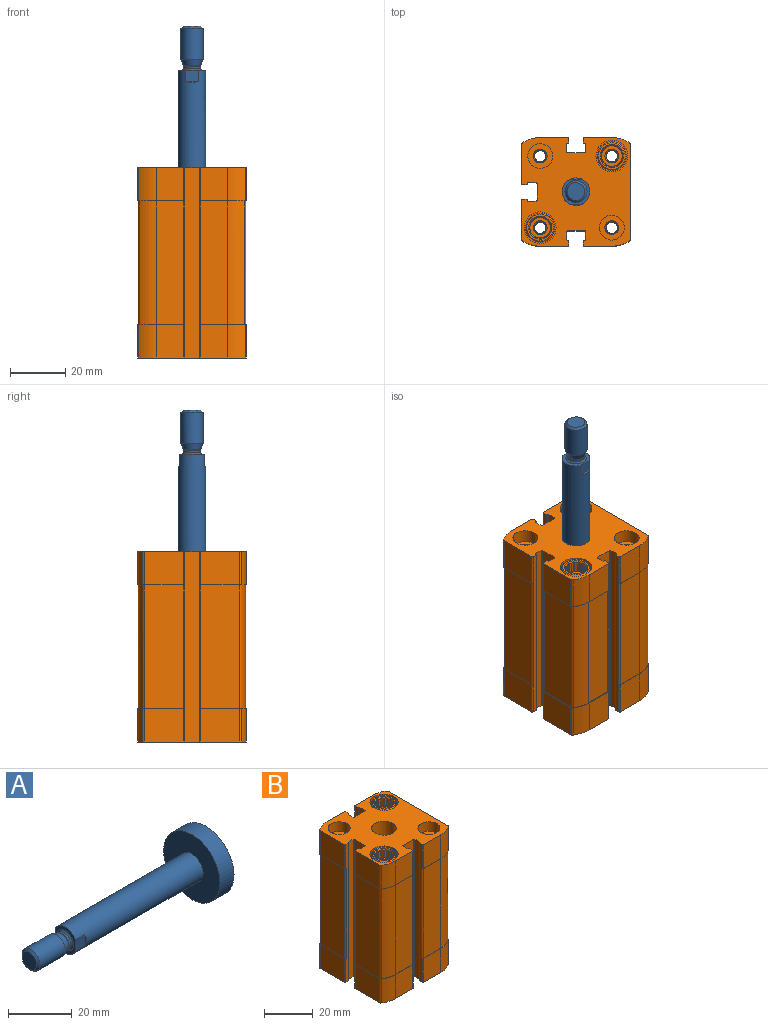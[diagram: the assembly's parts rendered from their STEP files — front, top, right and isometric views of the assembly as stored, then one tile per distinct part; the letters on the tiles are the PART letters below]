
ASSEMBLY  parts=2 mates=1
PART A: 16 faces, bbox 79.1x25.6x25.6 mm
  f0: plane 6.47x6.47mm, normal (-1,0,0), area 32.9mm2, adj f1
  f1: revolved ~8x8mm, area 24.6mm2, adj f0,f2
  f2: revolved ~11.26x8mm, area 283mm2, adj f1,f3
  f3: revolved ~8x8mm, area 56.6mm2, adj f2,f4
  f4: revolved ~6.27x6.27mm, area 4.1mm2, adj f3,f6
  f5: plane 25x25mm, normal (1,0,0), area 490.8mm2, adj f7
  f6: revolved ~6.2x6.2mm, area 15.5mm2, adj f4,f8
  f7: revolved ~25x25mm, area 490.9mm2, adj f5,f9
  f8: revolved ~7.4x7.4mm, area 19.7mm2, adj f6,f12
  f9: plane 25x25mm, normal (-1,0,0), area 412.4mm2, adj f7,f15
  f10: plane 4.94x1.08mm, normal (-0.87,0.5,0), area 1.7mm2, adj f11,f15
  f11: plane 4.36x4.2mm, normal (0,1,0), area 18.3mm2, adj f10,f12,f15
  f12: plane 10x9mm, normal (-1,0,0), area 32.6mm2, adj f8,f11,f13,f15
  f13: plane 4.36x4.2mm, normal (0,-1,0), area 18.3mm2, adj f12,f14,f15
  f14: plane 4.94x1.08mm, normal (-0.87,-0.5,0), area 1.7mm2, adj f13,f15
  f15: revolved ~56.25x10mm, area 1729.3mm2, adj f9,f10,f11,f12,f13,f14
PART B: 334 faces, bbox 39.6x39.6x69.1 mm
  f0: plane 1.01x0.59mm, normal (0,0,1), area 0.2mm2, adj f32,f33,f52
  f1: plane 1.01x0.59mm, normal (0,0,1), area 0.2mm2, adj f30,f31,f52
  f2: plane 1.17x0.34mm, normal (0,0,1), area 0.2mm2, adj f28,f29,f52
  f3: plane 1.01x0.59mm, normal (0,0,1), area 0.2mm2, adj f50,f51,f52
  f4: plane 1.01x0.59mm, normal (0,0,1), area 0.2mm2, adj f48,f49,f52
  f5: plane 1.17x0.34mm, normal (0,0,1), area 0.2mm2, adj f46,f47,f52
  f6: plane 1.01x0.59mm, normal (0,0,1), area 0.2mm2, adj f44,f45,f52
  f7: plane 1.01x0.59mm, normal (0,0,1), area 0.2mm2, adj f42,f43,f52
  f8: plane 1.17x0.34mm, normal (0,0,1), area 0.2mm2, adj f40,f41,f52
  f9: plane 1.01x0.59mm, normal (0,0,1), area 0.2mm2, adj f38,f39,f52
  f10: plane 1.01x0.59mm, normal (0,0,1), area 0.2mm2, adj f36,f37,f52
  f11: plane 1.17x0.34mm, normal (0,0,1), area 0.2mm2, adj f34,f35,f52
  f12: plane 1.01x0.59mm, normal (0,0,1), area 0.2mm2, adj f57,f58,f77
  f13: plane 1.01x0.59mm, normal (0,0,1), area 0.2mm2, adj f55,f56,f77
  f14: plane 1.17x0.34mm, normal (0,0,1), area 0.2mm2, adj f53,f54,f77
  f15: plane 1.01x0.59mm, normal (0,0,1), area 0.2mm2, adj f75,f76,f77
  f16: plane 1.01x0.59mm, normal (0,0,1), area 0.2mm2, adj f73,f74,f77
  f17: plane 1.17x0.34mm, normal (0,0,1), area 0.2mm2, adj f71,f72,f77
  f18: plane 1.01x0.59mm, normal (0,0,1), area 0.2mm2, adj f69,f70,f77
  f19: plane 1.01x0.59mm, normal (0,0,1), area 0.2mm2, adj f67,f68,f77
  f20: plane 1.17x0.34mm, normal (0,0,1), area 0.2mm2, adj f65,f66,f77
  f21: plane 1.01x0.59mm, normal (0,0,1), area 0.2mm2, adj f63,f64,f77
  f22: plane 1.01x0.59mm, normal (0,0,1), area 0.2mm2, adj f61,f62,f77
  f23: plane 1.17x0.34mm, normal (0,0,1), area 0.2mm2, adj f59,f60,f77
  f24: plane 7.5x7.5mm, normal (0,0,1), area 24.6mm2, adj f52,f78
  f25: plane 7.5x7.5mm, normal (0,0,1), area 24.6mm2, adj f77,f79
  f26: revolved ~14.47x4.13mm, area 187.9mm2, adj f27,f80
  f27: plane 5x5mm, normal (0,0,1), area 6.2mm2, adj f26,f81
  f28: plane 4.18x0.64mm, normal (0.5,-0.87,0), area 2.6mm2, adj f2,f29,f52,f82
  f29: plane 4.18x0.64mm, normal (-0.5,-0.87,0), area 2.6mm2, adj f2,f28,f52,f82
  f30: plane 4.18x0.73mm, normal (0,-1,0), area 2.6mm2, adj f1,f31,f52,f82
  f31: plane 4.18x0.64mm, normal (-0.87,-0.5,0), area 2.6mm2, adj f1,f30,f52,f82
  f32: plane 4.18x0.64mm, normal (-0.5,-0.87,0), area 2.6mm2, adj f0,f33,f52,f82
  f33: plane 4.18x0.73mm, normal (-1,0,0), area 2.6mm2, adj f0,f32,f52,f82
  f34: plane 4.18x0.64mm, normal (-0.87,-0.5,0), area 2.6mm2, adj f11,f35,f52,f82
  f35: plane 4.18x0.64mm, normal (-0.87,0.5,0), area 2.6mm2, adj f11,f34,f52,f82
  f36: plane 4.18x0.73mm, normal (-1,0,0), area 2.6mm2, adj f10,f37,f52,f82
  f37: plane 4.18x0.64mm, normal (-0.5,0.87,0), area 2.6mm2, adj f10,f36,f52,f82
  f38: plane 4.18x0.64mm, normal (-0.87,0.5,0), area 2.6mm2, adj f9,f39,f52,f82
  f39: plane 4.18x0.73mm, normal (0,1,0), area 2.6mm2, adj f9,f38,f52,f82
  f40: plane 4.18x0.64mm, normal (-0.5,0.87,0), area 2.6mm2, adj f8,f41,f52,f82
  f41: plane 4.18x0.64mm, normal (0.5,0.87,0), area 2.6mm2, adj f8,f40,f52,f82
  f42: plane 4.18x0.73mm, normal (0,1,0), area 2.6mm2, adj f7,f43,f52,f82
  f43: plane 4.18x0.64mm, normal (0.87,0.5,0), area 2.6mm2, adj f7,f42,f52,f82
  f44: plane 4.18x0.64mm, normal (0.5,0.87,0), area 2.6mm2, adj f6,f45,f52,f82
  f45: plane 4.18x0.73mm, normal (1,0,0), area 2.6mm2, adj f6,f44,f52,f82
  f46: plane 4.18x0.64mm, normal (0.87,0.5,0), area 2.6mm2, adj f5,f47,f52,f82
  f47: plane 4.18x0.64mm, normal (0.87,-0.5,0), area 2.6mm2, adj f5,f46,f52,f82
  f48: plane 4.18x0.73mm, normal (1,0,0), area 2.6mm2, adj f4,f49,f52,f82
  f49: plane 4.18x0.64mm, normal (0.5,-0.87,0), area 2.6mm2, adj f4,f48,f52,f82
  f50: plane 4.18x0.64mm, normal (0.87,-0.5,0), area 2.6mm2, adj f3,f51,f52,f82
  f51: plane 4.18x0.73mm, normal (0,-1,0), area 2.6mm2, adj f3,f50,f52,f82
  f52: revolved ~7.5x7.5mm, area 39.1mm2, adj f0,f1,f2,f3,f4,f5,f6,f7
  f53: plane 4.18x0.64mm, normal (0.5,-0.87,0), area 2.6mm2, adj f14,f54,f77,f83
  f54: plane 4.18x0.64mm, normal (-0.5,-0.87,0), area 2.6mm2, adj f14,f53,f77,f83
  f55: plane 4.18x0.73mm, normal (0,-1,0), area 2.6mm2, adj f13,f56,f77,f83
  f56: plane 4.18x0.64mm, normal (-0.87,-0.5,0), area 2.6mm2, adj f13,f55,f77,f83
  f57: plane 4.18x0.64mm, normal (-0.5,-0.87,0), area 2.6mm2, adj f12,f58,f77,f83
  f58: plane 4.18x0.73mm, normal (-1,0,0), area 2.6mm2, adj f12,f57,f77,f83
  f59: plane 4.18x0.64mm, normal (-0.87,-0.5,0), area 2.6mm2, adj f23,f60,f77,f83
  f60: plane 4.18x0.64mm, normal (-0.87,0.5,0), area 2.6mm2, adj f23,f59,f77,f83
  f61: plane 4.18x0.73mm, normal (-1,0,0), area 2.6mm2, adj f22,f62,f77,f83
  f62: plane 4.18x0.64mm, normal (-0.5,0.87,0), area 2.6mm2, adj f22,f61,f77,f83
  f63: plane 4.18x0.64mm, normal (-0.87,0.5,0), area 2.6mm2, adj f21,f64,f77,f83
  f64: plane 4.18x0.73mm, normal (0,1,0), area 2.6mm2, adj f21,f63,f77,f83
  f65: plane 4.18x0.64mm, normal (-0.5,0.87,0), area 2.6mm2, adj f20,f66,f77,f83
  f66: plane 4.18x0.64mm, normal (0.5,0.87,0), area 2.6mm2, adj f20,f65,f77,f83
  f67: plane 4.18x0.73mm, normal (0,1,0), area 2.6mm2, adj f19,f68,f77,f83
  f68: plane 4.18x0.64mm, normal (0.87,0.5,0), area 2.6mm2, adj f19,f67,f77,f83
  f69: plane 4.18x0.64mm, normal (0.5,0.87,0), area 2.6mm2, adj f18,f70,f77,f83
  f70: plane 4.18x0.73mm, normal (1,0,0), area 2.6mm2, adj f18,f69,f77,f83
  f71: plane 4.18x0.64mm, normal (0.87,0.5,0), area 2.6mm2, adj f17,f72,f77,f83
  f72: plane 4.18x0.64mm, normal (0.87,-0.5,0), area 2.6mm2, adj f17,f71,f77,f83
  f73: plane 4.18x0.73mm, normal (1,0,0), area 2.6mm2, adj f16,f74,f77,f83
  f74: plane 4.18x0.64mm, normal (0.5,-0.87,0), area 2.6mm2, adj f16,f73,f77,f83
  f75: plane 4.18x0.64mm, normal (0.87,-0.5,0), area 2.6mm2, adj f15,f76,f77,f83
  f76: plane 4.18x0.73mm, normal (0,-1,0), area 2.6mm2, adj f15,f75,f77,f83
  f77: revolved ~7.5x7.5mm, area 39.1mm2, adj f12,f13,f14,f15,f16,f17,f18,f19
  f78: revolved ~5x5mm, area 8.8mm2, adj f24,f84
  f79: revolved ~5x5mm, area 8.8mm2, adj f25,f85
  f80: revolved ~5x5mm, area 8.8mm2, adj f26,f86
  f81: revolved ~37.5x5mm, area 589mm2, adj f27,f99
  f82: revolved ~8.4x8.4mm, area 18.3mm2, adj f28,f29,f30,f31,f32,f33,f34,f35
  f83: revolved ~8.4x8.4mm, area 18.3mm2, adj f53,f54,f55,f56,f57,f58,f59,f60
  f84: revolved ~14.47x4.13mm, area 187.9mm2, adj f78,f102
  f85: revolved ~14.47x4.13mm, area 187.9mm2, adj f79,f103
  f86: plane 7.5x7.5mm, normal (0,0,-1), area 24.5mm2, adj f80,f126
  f87: plane 1.01x0.59mm, normal (0,0,-1), area 0.2mm2, adj f124,f125,f126
  f88: plane 1.17x0.34mm, normal (0,0,-1), area 0.2mm2, adj f122,f123,f126
  f89: plane 1.01x0.59mm, normal (0,0,-1), area 0.2mm2, adj f120,f121,f126
  f90: plane 1.01x0.59mm, normal (0,0,-1), area 0.2mm2, adj f118,f119,f126
  f91: plane 1.17x0.34mm, normal (0,0,-1), area 0.2mm2, adj f116,f117,f126
  f92: plane 1.01x0.59mm, normal (0,0,-1), area 0.2mm2, adj f114,f115,f126
  f93: plane 1.01x0.59mm, normal (0,0,-1), area 0.2mm2, adj f112,f113,f126
  f94: plane 1.17x0.34mm, normal (0,0,-1), area 0.2mm2, adj f110,f111,f126
  f95: plane 1.01x0.59mm, normal (0,0,-1), area 0.2mm2, adj f108,f109,f126
  f96: plane 1.01x0.59mm, normal (0,0,-1), area 0.2mm2, adj f106,f107,f126
  f97: plane 1.17x0.34mm, normal (0,0,-1), area 0.2mm2, adj f104,f105,f126
  f98: plane 1.01x0.59mm, normal (0,0,-1), area 0.2mm2, adj f126,f127,f128
  f99: plane 5x5mm, normal (0,0,-1), area 6.2mm2, adj f81,f130
  f100: plane 9.7x9.7mm, normal (0,0,1), area 18.5mm2, adj f82,f131
  f101: plane 9.7x9.7mm, normal (0,0,1), area 18.5mm2, adj f83,f132
  f102: plane 5x5mm, normal (0,0,-1), area 6.2mm2, adj f84,f134
  f103: plane 5x5mm, normal (0,0,-1), area 6.2mm2, adj f85,f135
  f104: plane 4.18x0.64mm, normal (0.87,-0.5,0), area 2.6mm2, adj f97,f105,f126,f136
  f105: plane 4.18x0.64mm, normal (0.87,0.5,0), area 2.6mm2, adj f97,f104,f126,f136
  f106: plane 4.18x0.73mm, normal (1,0,0), area 2.6mm2, adj f96,f107,f126,f136
  f107: plane 4.18x0.64mm, normal (0.5,0.87,0), area 2.6mm2, adj f96,f106,f126,f136
  f108: plane 4.18x0.64mm, normal (0.87,0.5,0), area 2.6mm2, adj f95,f109,f126,f136
  f109: plane 4.18x0.73mm, normal (0,1,0), area 2.6mm2, adj f95,f108,f126,f136
  f110: plane 4.18x0.64mm, normal (0.5,0.87,0), area 2.6mm2, adj f94,f111,f126,f136
  f111: plane 4.18x0.64mm, normal (-0.5,0.87,0), area 2.6mm2, adj f94,f110,f126,f136
  f112: plane 4.18x0.73mm, normal (0,1,0), area 2.6mm2, adj f93,f113,f126,f136
  f113: plane 4.18x0.64mm, normal (-0.87,0.5,0), area 2.6mm2, adj f93,f112,f126,f136
  f114: plane 4.18x0.64mm, normal (-0.5,0.87,0), area 2.6mm2, adj f92,f115,f126,f136
  f115: plane 4.18x0.73mm, normal (-1,0,0), area 2.6mm2, adj f92,f114,f126,f136
  f116: plane 4.18x0.64mm, normal (-0.87,0.5,0), area 2.6mm2, adj f91,f117,f126,f136
  f117: plane 4.18x0.64mm, normal (-0.87,-0.5,0), area 2.6mm2, adj f91,f116,f126,f136
  f118: plane 4.18x0.73mm, normal (-1,0,0), area 2.6mm2, adj f90,f119,f126,f136
  f119: plane 4.18x0.64mm, normal (-0.5,-0.87,0), area 2.6mm2, adj f90,f118,f126,f136
  f120: plane 4.18x0.64mm, normal (-0.87,-0.5,0), area 2.6mm2, adj f89,f121,f126,f136
  f121: plane 4.18x0.73mm, normal (0,-1,0), area 2.6mm2, adj f89,f120,f126,f136
  f122: plane 4.18x0.64mm, normal (-0.5,-0.87,0), area 2.6mm2, adj f88,f123,f126,f136
  f123: plane 4.18x0.64mm, normal (0.5,-0.87,0), area 2.6mm2, adj f88,f122,f126,f136
  f124: plane 4.18x0.73mm, normal (0,-1,0), area 2.6mm2, adj f87,f125,f126,f136
  f125: plane 4.18x0.64mm, normal (0.87,-0.5,0), area 2.6mm2, adj f87,f124,f126,f136
  f126: revolved ~7.5x7.5mm, area 39.1mm2, adj f86,f87,f88,f89,f90,f91,f92,f93
  f127: plane 4.18x0.64mm, normal (0.5,-0.87,0), area 2.6mm2, adj f98,f126,f128,f136
  f128: plane 4.18x0.73mm, normal (1,0,0), area 2.6mm2, adj f98,f126,f127,f136
  f129: plane 4.14x4.14mm, normal (1,0,0), area 13.4mm2, adj f137
  f130: revolved ~6.77x4.13mm, area 87.9mm2, adj f99,f138
  f131: revolved ~10.5x10.5mm, area 17.9mm2, adj f100,f139
  f132: revolved ~10.5x10.5mm, area 17.9mm2, adj f101,f140
  f133: plane 25x25mm, normal (0,0,1), area 490.9mm2, adj f141
  f134: revolved ~37.5x5mm, area 589mm2, adj f102,f142
  f135: revolved ~37.5x5mm, area 589mm2, adj f103,f143
  f136: revolved ~8.4x8.4mm, area 18.3mm2, adj f104,f105,f106,f107,f108,f109,f110,f111
  f137: revolved ~10.57x4.13mm, area 137.2mm2, adj f129,f146
  f138: revolved ~5x5mm, area 8.8mm2, adj f130,f147
  f139: revolved ~10.5x10.5mm, area 201.2mm2, adj f131,f148
  f140: revolved ~10.5x10.5mm, area 201.2mm2, adj f132,f149
  f141: revolved ~36.25x25mm, area 2847.1mm2, adj f133,f150
  f142: plane 5x5mm, normal (0,0,1), area 6.2mm2, adj f134,f151
  f143: plane 5x5mm, normal (0,0,1), area 6.2mm2, adj f135,f152
  f144: plane 9.7x9.7mm, normal (0,0,-1), area 18.5mm2, adj f136,f153
  f145: plane 4.14x4.14mm, normal (1,0,0), area 13.4mm2, adj f159
  f146: revolved ~5x5mm, area 8.8mm2, adj f137,f174
  f147: plane 9x9mm, normal (0,0,1), area 44mm2, adj f138,f182
  f148: plane 11.5x11.5mm, normal (0,0,1), area 17.3mm2, adj f139,f184
  f149: plane 11.5x11.5mm, normal (0,0,1), area 17.3mm2, adj f140,f185
  f150: plane 25x25mm, normal (0,0,-1), area 412.3mm2, adj f141,f186
  f151: revolved ~6.77x4.13mm, area 87.9mm2, adj f142,f193
  f152: revolved ~6.77x4.13mm, area 87.9mm2, adj f143,f194
  f153: revolved ~10.5x10.5mm, area 35.9mm2, adj f144,f195
  f154: plane 45x13.99mm, normal (-1,0,0), area 629.6mm2, adj f155,f157,f199,f201
  f155: revolved ~45x0.68mm, area 36.7mm2, adj f154,f156,f157,f201
  f156: revolved ~45x6.12mm, area 289.7mm2, adj f155,f157,f158,f201
  f157: plane 17.05x17.05mm, normal (0,0,-1), area 8mm2, adj f154,f155,f156,f158,f178,f179,f180,f181
  f158: plane 45x9.9mm, normal (0,1,0), area 445.5mm2, adj f156,f157,f201,f203
  f159: revolved ~10.57x4.13mm, area 137.2mm2, adj f145,f206
  f160: plane 45x9.9mm, normal (0,1,0), area 445.5mm2, adj f161,f166,f204,f207
  f161: revolved ~45x6.12mm, area 289.7mm2, adj f160,f162,f166,f207
  f162: revolved ~45x0.68mm, area 36.7mm2, adj f161,f163,f166,f207
  f163: plane 45x34.18mm, normal (1,0,0), area 1538.2mm2, adj f162,f164,f166,f207
  f164: revolved ~45x0.68mm, area 36.7mm2, adj f163,f165,f166,f207
  f165: revolved ~45x6.12mm, area 289.7mm2, adj f164,f166,f167,f207
  f166: plane 39.5x17.05mm, normal (0,0,-1), area 17.3mm2, adj f160,f161,f162,f163,f164,f165,f167,f171
  f167: plane 45x9.9mm, normal (0,-1,0), area 445.5mm2, adj f165,f166,f207,f209
  f168: plane 14.08x12mm, normal (-1,0,0), area 169mm2, adj f169,f187,f197,f211
  f169: revolved ~12x0.67mm, area 9.5mm2, adj f168,f170,f187,f211
  f170: revolved ~12x6.39mm, area 81.1mm2, adj f169,f187,f188,f211
  f171: plane 12x9.9mm, normal (0,-1,0), area 118.8mm2, adj f166,f172,f208,f211
  f172: revolved ~12x6.39mm, area 81.1mm2, adj f166,f171,f173,f211
  f173: revolved ~12x0.67mm, area 9.5mm2, adj f166,f172,f174,f211
  f174: plane 34.37x12mm, normal (1,0,0), area 392.8mm2, adj f146,f166,f173,f175,f211
  f175: revolved ~12x0.67mm, area 9.5mm2, adj f166,f174,f176,f211
  f176: revolved ~12x6.39mm, area 81.1mm2, adj f166,f175,f177,f211
  f177: plane 12x9.9mm, normal (0,1,0), area 118.8mm2, adj f166,f176,f205,f211
  f178: plane 12x9.9mm, normal (0,1,0), area 118.8mm2, adj f157,f179,f202,f211
  f179: revolved ~12x6.39mm, area 81.1mm2, adj f157,f178,f180,f211
  f180: revolved ~12x0.67mm, area 9.5mm2, adj f157,f179,f181,f211
  f181: plane 14.08x12mm, normal (-1,0,0), area 169mm2, adj f157,f180,f200,f211
  f182: revolved ~9x9mm, area 135.7mm2, adj f147,f211
  f183: revolved ~9x9mm, area 135.7mm2, adj f196,f211
  f184: revolved ~11.5x11.5mm, area 234.8mm2, adj f148,f211
  f185: revolved ~11.5x11.5mm, area 234.8mm2, adj f149,f211
  f186: revolved ~20.75x10mm, area 651.9mm2, adj f150,f211
  f187: plane 17.05x17.05mm, normal (0,0,-1), area 8mm2, adj f168,f169,f170,f188,f189,f190,f191,f192
  f188: plane 12x9.9mm, normal (0,-1,0), area 118.8mm2, adj f170,f187,f211,f212
  f189: plane 45x9.9mm, normal (0,-1,0), area 445.5mm2, adj f187,f190,f210,f213
  f190: revolved ~45x6.12mm, area 289.7mm2, adj f187,f189,f191,f213
  f191: revolved ~45x0.68mm, area 36.7mm2, adj f187,f190,f192,f213
  f192: plane 45x13.99mm, normal (-1,0,0), area 629.6mm2, adj f187,f191,f198,f213
  f193: revolved ~5x5mm, area 8.8mm2, adj f151,f214
  f194: revolved ~5x5mm, area 8.8mm2, adj f152,f215
  f195: revolved ~10.5x10.5mm, area 201.2mm2, adj f153,f216
  f196: plane 9x9mm, normal (0,0,1), area 44mm2, adj f183,f218
  f197: revolved ~12x0.4mm, area 7.5mm2, adj f168,f187,f211,f220
  f198: revolved ~45x0.4mm, area 28.3mm2, adj f187,f192,f213,f220
  f199: revolved ~45x0.4mm, area 28.3mm2, adj f154,f157,f201,f232
  f200: revolved ~12x0.4mm, area 7.5mm2, adj f157,f181,f211,f232
  f201: plane 17.05x17.05mm, normal (0,0,1), area 8mm2, adj f154,f155,f156,f158,f199,f203,f232,f233
  f202: revolved ~12x0.4mm, area 7.5mm2, adj f157,f178,f211,f239
  f203: revolved ~45x0.4mm, area 28.3mm2, adj f157,f158,f201,f239
  f204: revolved ~45x0.4mm, area 28.3mm2, adj f160,f166,f207,f251
  f205: revolved ~12x0.4mm, area 7.5mm2, adj f166,f177,f211,f251
  f206: revolved ~5x5mm, area 8.8mm2, adj f159,f256
  f207: plane 39.5x17.05mm, normal (0,0,1), area 17.3mm2, adj f160,f161,f162,f163,f164,f165,f167,f204
  f208: revolved ~12x0.4mm, area 7.5mm2, adj f166,f171,f211,f261
  f209: revolved ~45x0.4mm, area 28.3mm2, adj f166,f167,f207,f261
  f210: revolved ~45x0.4mm, area 28.3mm2, adj f187,f189,f213,f273
  f211: plane 39.5x39.5mm, normal (0,0,1), area 1022.2mm2, adj f168,f169,f170,f171,f172,f173,f174,f175
  f212: revolved ~12x0.4mm, area 7.5mm2, adj f187,f188,f211,f273
  f213: plane 17.05x17.05mm, normal (0,0,1), area 8mm2, adj f189,f190,f191,f192,f198,f210,f219,f220
  f214: plane 9x9mm, normal (0,0,-1), area 44mm2, adj f193,f279
  f215: plane 9x9mm, normal (0,0,-1), area 44mm2, adj f194,f280
  f216: plane 11.5x11.5mm, normal (0,0,-1), area 17.3mm2, adj f195,f281
  f217: plane 9x9mm, normal (0,0,-1), area 63.6mm2, adj f282
  f218: revolved ~5x5mm, area 8.8mm2, adj f196,f283
  f219: revolved ~12x0.4mm, area 7.5mm2, adj f213,f220,f278,f284
  f220: plane 69x1.65mm, normal (0,1,0), area 102.6mm2, adj f187,f197,f198,f211,f213,f219,f221,f284
  f221: revolved ~69x0.2mm, area 21.7mm2, adj f211,f220,f222,f284
  f222: plane 69x0.3mm, normal (1,0,0), area 20.7mm2, adj f211,f221,f223,f284
  f223: revolved ~69x0.2mm, area 21.7mm2, adj f211,f222,f224,f284
  f224: plane 69x2.8mm, normal (0,1,0), area 193.2mm2, adj f211,f223,f225,f284
  f225: revolved ~69x0.4mm, area 43.4mm2, adj f211,f224,f226,f284
  f226: plane 69x6mm, normal (-1,0,0), area 414mm2, adj f211,f225,f227,f284
  f227: revolved ~69x0.4mm, area 43.4mm2, adj f211,f226,f228,f284
  f228: plane 69x2.8mm, normal (0,-1,0), area 193.2mm2, adj f211,f227,f229,f284
  f229: revolved ~69x0.2mm, area 21.7mm2, adj f211,f228,f230,f284
  f230: plane 69x0.3mm, normal (1,0,0), area 20.7mm2, adj f211,f229,f231,f284
  f231: revolved ~69x0.2mm, area 21.7mm2, adj f211,f230,f232,f284
  f232: plane 69x1.65mm, normal (0,-1,0), area 102.6mm2, adj f157,f199,f200,f201,f211,f231,f233,f284
  f233: revolved ~12x0.4mm, area 7.5mm2, adj f201,f232,f234,f284
  f234: plane 14.08x12mm, normal (-1,0,0), area 169mm2, adj f201,f233,f235,f284
  f235: revolved ~12x0.67mm, area 9.5mm2, adj f201,f234,f236,f284
  f236: revolved ~12x6.39mm, area 81.1mm2, adj f201,f235,f237,f284
  f237: plane 12x9.9mm, normal (0,1,0), area 118.8mm2, adj f201,f236,f238,f284
  f238: revolved ~12x0.4mm, area 7.5mm2, adj f201,f237,f239,f284
  f239: plane 69x1.65mm, normal (1,0,0), area 102.6mm2, adj f157,f201,f202,f203,f211,f238,f240,f284
  f240: revolved ~69x0.2mm, area 21.7mm2, adj f211,f239,f241,f284
  f241: plane 69x0.3mm, normal (0,-1,0), area 20.7mm2, adj f211,f240,f242,f284
  f242: revolved ~69x0.2mm, area 21.7mm2, adj f211,f241,f243,f284
  f243: plane 69x2.8mm, normal (1,0,0), area 193.2mm2, adj f211,f242,f244,f284
  f244: revolved ~69x0.4mm, area 43.4mm2, adj f211,f243,f245,f284
  f245: plane 69x6mm, normal (0,1,0), area 414mm2, adj f211,f244,f246,f284
  f246: revolved ~69x0.4mm, area 43.4mm2, adj f211,f245,f247,f284
  f247: plane 69x2.8mm, normal (-1,0,0), area 193.2mm2, adj f211,f246,f248,f284
  f248: revolved ~69x0.2mm, area 21.7mm2, adj f211,f247,f249,f284
  f249: plane 69x0.3mm, normal (0,-1,0), area 20.7mm2, adj f211,f248,f250,f284
  f250: revolved ~69x0.2mm, area 21.7mm2, adj f211,f249,f251,f284
  f251: plane 69x1.65mm, normal (-1,0,0), area 102.6mm2, adj f166,f204,f205,f207,f211,f250,f252,f284
  f252: revolved ~12x0.4mm, area 7.5mm2, adj f207,f251,f253,f284
  f253: plane 12x9.9mm, normal (0,1,0), area 118.8mm2, adj f207,f252,f254,f284
  f254: revolved ~12x6.39mm, area 81.1mm2, adj f207,f253,f255,f284
  f255: revolved ~12x0.67mm, area 9.5mm2, adj f207,f254,f256,f284
  f256: plane 34.37x12mm, normal (1,0,0), area 392.8mm2, adj f206,f207,f255,f257,f284
  f257: revolved ~12x0.67mm, area 9.5mm2, adj f207,f256,f258,f284
  f258: revolved ~12x6.39mm, area 81.1mm2, adj f207,f257,f259,f284
  f259: plane 12x9.9mm, normal (0,-1,0), area 118.8mm2, adj f207,f258,f260,f284
  f260: revolved ~12x0.4mm, area 7.5mm2, adj f207,f259,f261,f284
  f261: plane 69x1.65mm, normal (-1,0,0), area 102.6mm2, adj f166,f207,f208,f209,f211,f260,f262,f284
  f262: revolved ~69x0.2mm, area 21.7mm2, adj f211,f261,f263,f284
  f263: plane 69x0.3mm, normal (0,1,0), area 20.7mm2, adj f211,f262,f264,f284
  f264: revolved ~69x0.2mm, area 21.7mm2, adj f211,f263,f265,f284
  f265: plane 69x2.8mm, normal (-1,0,0), area 193.2mm2, adj f211,f264,f266,f284
  f266: revolved ~69x0.4mm, area 43.4mm2, adj f211,f265,f267,f284
  f267: plane 69x6mm, normal (0,-1,0), area 414mm2, adj f211,f266,f268,f284
  f268: revolved ~69x0.4mm, area 43.4mm2, adj f211,f267,f269,f284
  f269: plane 69x2.8mm, normal (1,0,0), area 193.2mm2, adj f211,f268,f270,f284
  f270: revolved ~69x0.2mm, area 21.7mm2, adj f211,f269,f271,f284
  f271: plane 69x0.3mm, normal (0,1,0), area 20.7mm2, adj f211,f270,f272,f284
  f272: revolved ~69x0.2mm, area 21.7mm2, adj f211,f271,f273,f284
  f273: plane 69x1.65mm, normal (1,0,0), area 102.6mm2, adj f187,f210,f211,f212,f213,f272,f274,f284
  f274: revolved ~12x0.4mm, area 7.5mm2, adj f213,f273,f275,f284
  f275: plane 12x9.9mm, normal (0,-1,0), area 118.8mm2, adj f213,f274,f276,f284
  f276: revolved ~12x6.39mm, area 81.1mm2, adj f213,f275,f277,f284
  f277: revolved ~12x0.67mm, area 9.5mm2, adj f213,f276,f278,f284
  f278: plane 14.08x12mm, normal (-1,0,0), area 169mm2, adj f213,f219,f277,f284
  f279: revolved ~9x9mm, area 135.7mm2, adj f214,f284
  f280: revolved ~9x9mm, area 135.7mm2, adj f215,f284
  f281: revolved ~11.5x11.5mm, area 234.8mm2, adj f216,f284
  f282: revolved ~9x9mm, area 59.4mm2, adj f217,f284
  f283: revolved ~6.77x4.13mm, area 87.9mm2, adj f218,f285
  f284: plane 39.5x39.5mm, normal (0,0,-1), area 1037.3mm2, adj f219,f220,f221,f222,f223,f224,f225,f226
  f285: plane 5x5mm, normal (0,0,-1), area 6.2mm2, adj f283,f287
  f286: revolved ~11.5x11.5mm, area 234.8mm2, adj f284,f288
  f287: revolved ~37.5x5mm, area 589mm2, adj f285,f289
  f288: plane 11.5x11.5mm, normal (0,0,-1), area 17.3mm2, adj f286,f290
  f289: plane 5x5mm, normal (0,0,1), area 6.2mm2, adj f287,f291
  f290: revolved ~10.5x10.5mm, area 201.2mm2, adj f288,f292
  f291: revolved ~14.47x4.13mm, area 187.9mm2, adj f289,f293
  f292: revolved ~10.5x10.5mm, area 17.9mm2, adj f290,f294
  f293: revolved ~5x5mm, area 8.8mm2, adj f291,f295
  f294: plane 9.7x9.7mm, normal (0,0,-1), area 18.5mm2, adj f292,f330
  f295: plane 7.5x7.5mm, normal (0,0,-1), area 24.5mm2, adj f293,f333
  f296: plane 4.18x0.64mm, normal (0.87,-0.5,0), area 2.6mm2, adj f330,f331,f332,f333
  f297: plane 4.18x0.73mm, normal (1,0,0), area 2.6mm2, adj f298,f299,f330,f333
  f298: plane 1.01x0.59mm, normal (0,0,-1), area 0.2mm2, adj f297,f299,f333
  f299: plane 4.18x0.64mm, normal (0.5,-0.87,0), area 2.6mm2, adj f297,f298,f330,f333
  f300: plane 4.18x0.64mm, normal (0.87,-0.5,0), area 2.6mm2, adj f301,f302,f330,f333
  f301: plane 1.01x0.59mm, normal (0,0,-1), area 0.2mm2, adj f300,f302,f333
  f302: plane 4.18x0.73mm, normal (0,-1,0), area 2.6mm2, adj f300,f301,f330,f333
  f303: plane 4.18x0.64mm, normal (0.5,-0.87,0), area 2.6mm2, adj f304,f305,f330,f333
  f304: plane 1.17x0.34mm, normal (0,0,-1), area 0.2mm2, adj f303,f305,f333
  f305: plane 4.18x0.64mm, normal (-0.5,-0.87,0), area 2.6mm2, adj f303,f304,f330,f333
  f306: plane 4.18x0.73mm, normal (0,-1,0), area 2.6mm2, adj f307,f308,f330,f333
  f307: plane 1.01x0.59mm, normal (0,0,-1), area 0.2mm2, adj f306,f308,f333
  f308: plane 4.18x0.64mm, normal (-0.87,-0.5,0), area 2.6mm2, adj f306,f307,f330,f333
  f309: plane 4.18x0.64mm, normal (-0.5,-0.87,0), area 2.6mm2, adj f310,f311,f330,f333
  f310: plane 1.01x0.59mm, normal (0,0,-1), area 0.2mm2, adj f309,f311,f333
  f311: plane 4.18x0.73mm, normal (-1,0,0), area 2.6mm2, adj f309,f310,f330,f333
  f312: plane 4.18x0.64mm, normal (-0.87,-0.5,0), area 2.6mm2, adj f313,f314,f330,f333
  f313: plane 1.17x0.34mm, normal (0,0,-1), area 0.2mm2, adj f312,f314,f333
  f314: plane 4.18x0.64mm, normal (-0.87,0.5,0), area 2.6mm2, adj f312,f313,f330,f333
  f315: plane 4.18x0.73mm, normal (-1,0,0), area 2.6mm2, adj f316,f317,f330,f333
  f316: plane 1.01x0.59mm, normal (0,0,-1), area 0.2mm2, adj f315,f317,f333
  f317: plane 4.18x0.64mm, normal (-0.5,0.87,0), area 2.6mm2, adj f315,f316,f330,f333
  f318: plane 4.18x0.64mm, normal (-0.87,0.5,0), area 2.6mm2, adj f319,f320,f330,f333
  f319: plane 1.01x0.59mm, normal (0,0,-1), area 0.2mm2, adj f318,f320,f333
  f320: plane 4.18x0.73mm, normal (0,1,0), area 2.6mm2, adj f318,f319,f330,f333
  f321: plane 4.18x0.64mm, normal (-0.5,0.87,0), area 2.6mm2, adj f322,f323,f330,f333
  f322: plane 1.17x0.34mm, normal (0,0,-1), area 0.2mm2, adj f321,f323,f333
  f323: plane 4.18x0.64mm, normal (0.5,0.87,0), area 2.6mm2, adj f321,f322,f330,f333
  f324: plane 4.18x0.73mm, normal (0,1,0), area 2.6mm2, adj f325,f326,f330,f333
  f325: plane 1.01x0.59mm, normal (0,0,-1), area 0.2mm2, adj f324,f326,f333
  f326: plane 4.18x0.64mm, normal (0.87,0.5,0), area 2.6mm2, adj f324,f325,f330,f333
  f327: plane 4.18x0.64mm, normal (0.5,0.87,0), area 2.6mm2, adj f328,f329,f330,f333
  f328: plane 1.01x0.59mm, normal (0,0,-1), area 0.2mm2, adj f327,f329,f333
  f329: plane 4.18x0.73mm, normal (1,0,0), area 2.6mm2, adj f327,f328,f330,f333
  f330: revolved ~8.4x8.4mm, area 18.3mm2, adj f294,f296,f297,f299,f300,f302,f303,f305
  f331: plane 4.18x0.64mm, normal (0.87,0.5,0), area 2.6mm2, adj f296,f330,f332,f333
  f332: plane 1.17x0.34mm, normal (0,0,-1), area 0.2mm2, adj f296,f331,f333
  f333: revolved ~7.5x7.5mm, area 39.1mm2, adj f295,f296,f297,f298,f299,f300,f301,f302
PLACE A rot(axis=(0.71,0,-0.71),180deg) t=(0,0,30)mm
PLACE B at identity
MATE slider A.f9 <-> B.f150  axis (0,0,1) through (0,0,-20.75)mm
